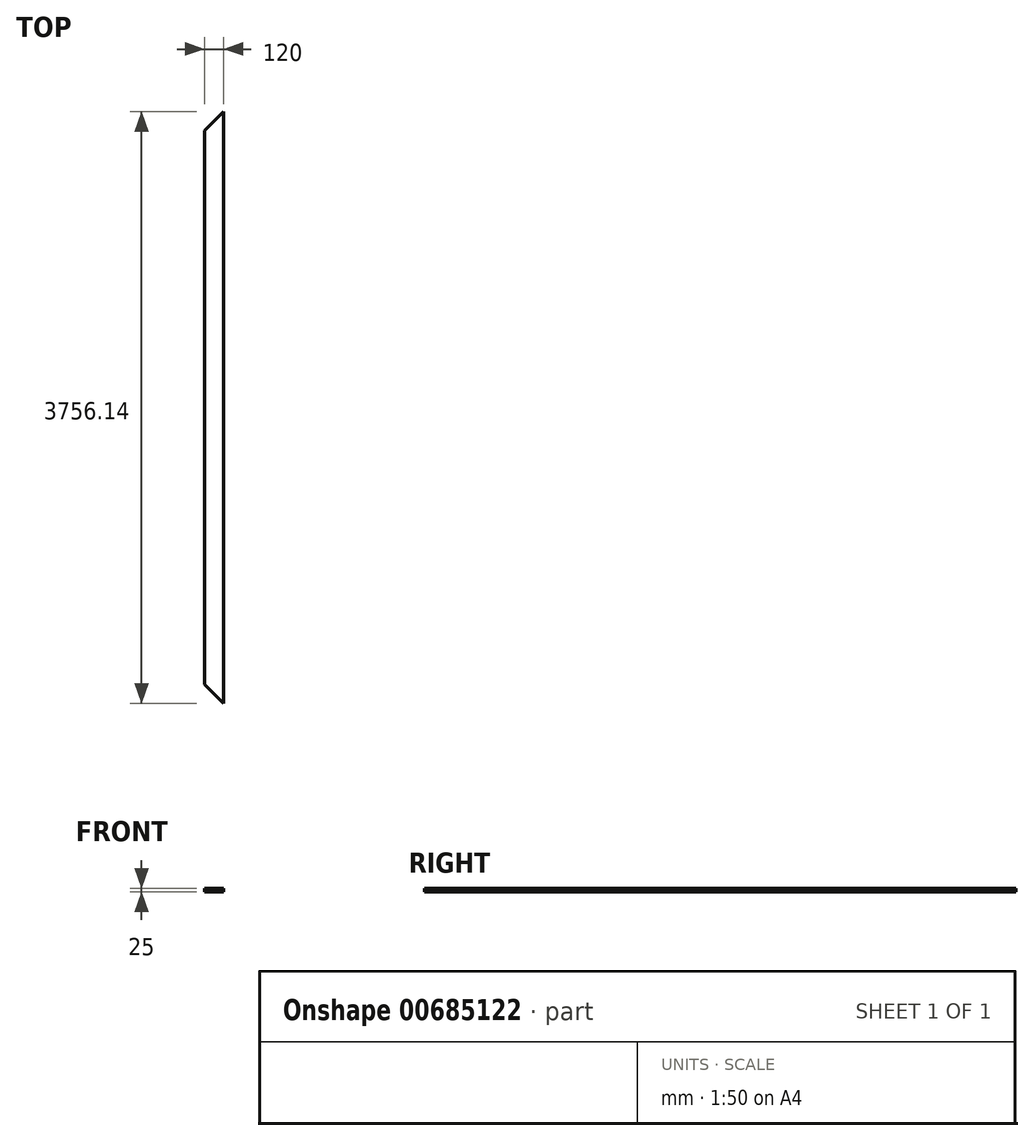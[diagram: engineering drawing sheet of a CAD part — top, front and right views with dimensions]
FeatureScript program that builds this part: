
annotation { "Feature Type Name" : "Feature", "Feature Type Description" : "" }
export const myFeature = defineFeature(function(context is Context, id is Id, definition is map)
    precondition{}
    {
        {
            var Q0;
            Q0=qCreatedBy(makeId("Top.planeOp"),FACE);
            var sketch = newSketch(context, id + "F0", { "sketchPlane" : qUnion([Q0])});
            skLineSegment(sketch, "E0", {"start": v(-4559.4, -3805.27) * mm, "end": v(-4559.4, 6093.58) * mm});
            skLineSegment(sketch, "E1", {"start": v(-4559.4, 6093.58) * mm, "end": v(4440.6, 6093.58) * mm});
            skLineSegment(sketch, "E2", {"start": v(4440.6, 6093.58) * mm, "end": v(4440.6, 2093.58) * mm});
            skLineSegment(sketch, "E3", {"start": v(4440.6, 2093.58) * mm, "end": v(-560.68, 2093.58) * mm});
            skLineSegment(sketch, "E4", {"start": v(-560.68, 2093.58) * mm, "end": v(-560.68, -3906.42) * mm});
            skLineSegment(sketch, "E5", {"start": v(-560.68, -3906.42) * mm, "end": v(-4559.4, -3805.27) * mm});
            skLineSegment(sketch, "E6", {"start": v(4440.6, 2093.58) * mm, "end": v(440.6, 6093.58) * mm});
            skLineSegment(sketch, "E7", {"start": v(4440.6, 6093.58) * mm, "end": v(440.6, 2093.58) * mm});
            skLineSegment(sketch, "E8", {"start": v(4440.6, 6092.45) * mm, "end": v(4440.6, 2094.71) * mm});
            skLineSegment(sketch, "E9", {"start": v(4440.6, 2094.71) * mm, "end": v(4320.6, 2214.71) * mm});
            skLineSegment(sketch, "E10", {"start": v(4320.6, 2214.71) * mm, "end": v(4320.6, 5972.45) * mm});
            skLineSegment(sketch, "E11", {"start": v(4320.6, 5972.45) * mm, "end": v(4440.6, 6092.45) * mm});
            skLineSegment(sketch, "E12", {"start": v(4319.8, 5971.65) * mm, "end": v(4319.8, 2215.51) * mm});
            skLineSegment(sketch, "E13", {"start": v(4319.8, 2215.51) * mm, "end": v(4199.8, 2335.51) * mm});
            skLineSegment(sketch, "E14", {"start": v(4199.8, 2335.51) * mm, "end": v(4199.8, 5851.65) * mm});
            skLineSegment(sketch, "E15", {"start": v(4199.8, 5851.65) * mm, "end": v(4319.8, 5971.65) * mm});
            skSolve(sketch);
        }
        {
            var Q0;
            Q0=makeQuery(id+"F0.imprint","IMPRINT",FACE,{"disambiguationData":[TD([[makeQuery(id+"F0.imprint","IMPRINT",EDGE,{"derivedFrom":sQuery(id+"F0.wireOp",EDGE,"E12")}),-1.0]])]});
            var Q1;
            Q1=makeQuery(id+"F0.imprint","IMPRINT",FACE,{"disambiguationData":[TD([[makeQuery(id+"F0.imprint","IMPRINT",EDGE,{"derivedFrom":sQuery(id+"F0.wireOp",EDGE,"E8")}),-1.0]])]});
            extrude(context, id + "F1", {"entities" : qUnion([Q0, Q1]), "oppositeDirection" : true, "depth" : 25 * mm, "offsetDistance" : 25 * mm});
        }
    });
